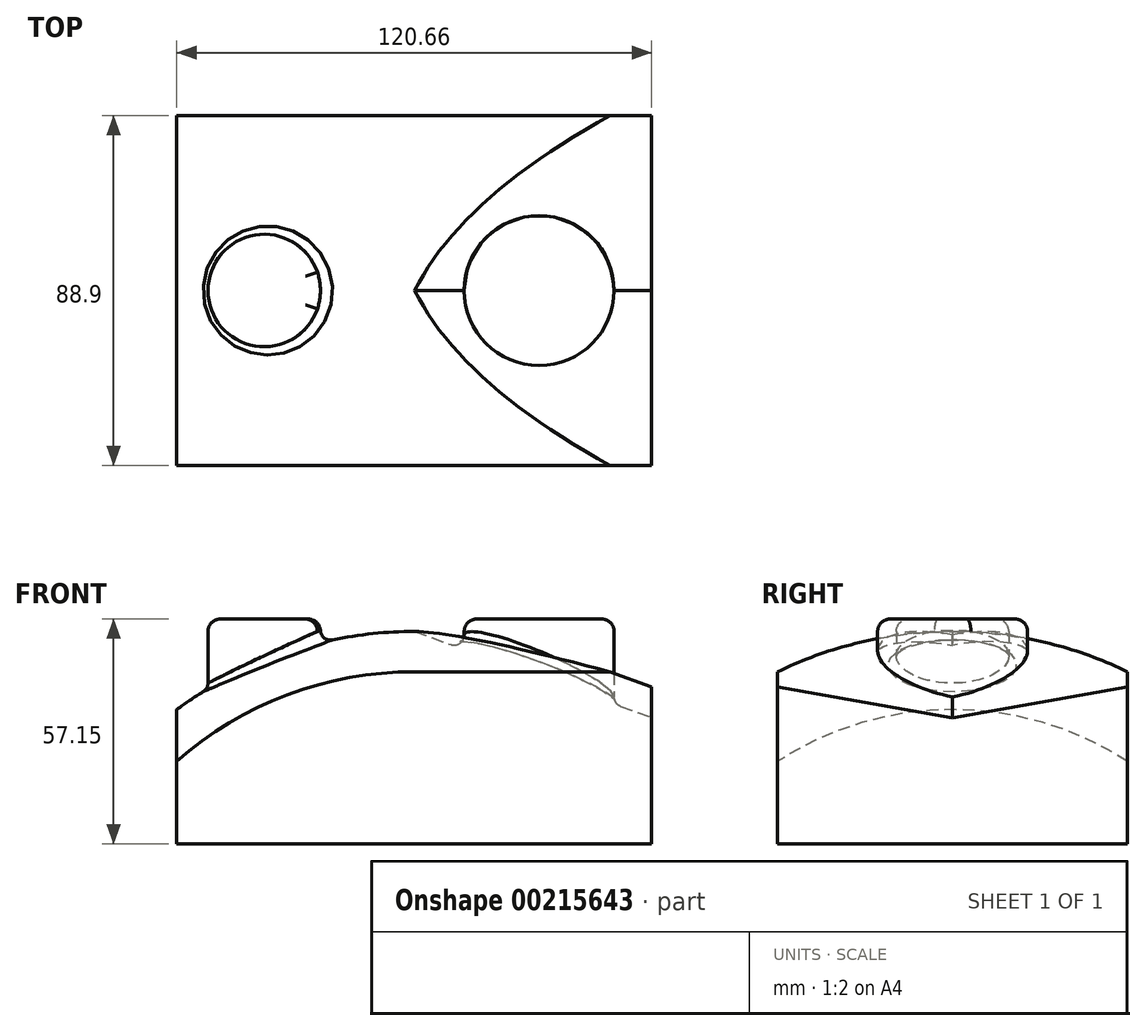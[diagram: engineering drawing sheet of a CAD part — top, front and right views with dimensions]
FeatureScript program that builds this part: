
annotation { "Feature Type Name" : "Feature", "Feature Type Description" : "" }
export const myFeature = defineFeature(function(context is Context, id is Id, definition is map)
    precondition{}
    {
        {
            var Q0;
            Q0=qCreatedBy(makeId("Top.planeOp"),FACE);
            var sketch = newSketch(context, id + "F0", { "sketchPlane" : qUnion([Q0])});
            skLineSegment(sketch, "E0.bottom", {"start": v(60.33, -44.45) * mm, "end": v(-60.33, -44.45) * mm});
            skLineSegment(sketch, "E0.top", {"start": v(60.33, 44.45) * mm, "end": v(-60.33, 44.45) * mm});
            skLineSegment(sketch, "E0.left", {"start": v(60.33, -44.45) * mm, "end": v(60.33, 44.45) * mm});
            skLineSegment(sketch, "E0.right", {"start": v(-60.33, -44.45) * mm, "end": v(-60.33, 44.45) * mm});
            skPoint(sketch, "E0.middle", {"position": v(0, 0) * mm});
            skSolve(sketch);
        }
        {
            var Q0;
            Q0 = qSketchRegion(id + "F0", true);
            extrude(context, id + "F1", {"entities" : qUnion([Q0]), "depth" : 53.97 * mm});
        }
        {
            var Q0;
            Q0=qCreatedBy(makeId("Front.planeOp"),FACE);
            var sketch = newSketch(context, id + "F2", { "sketchPlane" : qUnion([Q0])});
            skLineSegment(sketch, "E1", {"start": v(106.64, 12.85) * mm, "end": v(-12.7, 56.29) * mm});
            skSolve(sketch);
        }
        {
            var Q0;
            Q0=qCreatedBy(makeId("Right.planeOp"),FACE);
            var Q1;
            Q1=sQuery(id+"F2.wireOp",VERTEX,"E1.end");
            cPlane(context, id + "F3", {"entities" : qUnion([Q0, Q1]), "cplaneType" : CPlaneType.PLANE_POINT, "offset" : 25.4 * mm, "width" : 152.4 * mm, "height" : 152.4 * mm});
        }
        {
            var Q0;
            Q0=qCreatedBy(id+"F3.planeOp",FACE);
            var sketch = newSketch(context, id + "F4", { "sketchPlane" : qUnion([Q0])});
            skLineSegment(sketch, "E2", {"start": v(0, 58.65) * mm, "end": v(63.52, 69.85) * mm});
            skLineSegment(sketch, "E3", {"start": v(-63.52, 69.85) * mm, "end": v(0, 58.65) * mm});
            skLineSegment(sketch, "E4", {"start": v(-63.52, 69.85) * mm, "end": v(-63.52, 114.3) * mm});
            skLineSegment(sketch, "E5", {"start": v(-63.52, 114.3) * mm, "end": v(63.48, 114.3) * mm});
            skLineSegment(sketch, "E6", {"start": v(63.48, 114.3) * mm, "end": v(63.52, 69.85) * mm});
            skSolve(sketch);
        }
        {
            var Q0;
            Q0 = qSketchRegion(id + "F4", true);
            var Q1;
            Q1 = qConstructionFilter(qBodyType(qCreatedBy(id + "F2" ,EDGE), BodyType.WIRE), ConstructionObject.NO);
            sweep(context, id + "F5", {"operationType" : NewBodyOperationType.REMOVE, "profiles" : qUnion([Q0]), "path" : qUnion([Q1])});
        }
        {
            var Q0;
            Q0=qCreatedBy(makeId("Front.planeOp"),FACE);
            var sketch = newSketch(context, id + "F6", { "sketchPlane" : qUnion([Q0])});
            skArc(sketch, "E7", {"start": v(0, 53.98) * mm, "mid": v(-41.8, 44.98) * mm, "end": v(-76.2, 19.58) * mm});
            skLineSegment(sketch, "E8", {"start": v(0, 71.33) * mm, "end": v(0, 13.76) * mm, "construction": true});
            skLineSegment(sketch, "E9", {"start": v(0, 53.98) * mm, "end": v(0, 66.67) * mm});
            skLineSegment(sketch, "E10", {"start": v(0, 66.67) * mm, "end": v(-76.2, 66.67) * mm});
            skLineSegment(sketch, "E11", {"start": v(-76.2, 66.67) * mm, "end": v(-76.2, 19.58) * mm});
            skSolve(sketch);
        }
        {
            var Q0;
            Q0 = qSketchRegion(id + "F6", true);
            var Q1;
            Q1=sQuery(id+"F6.wireOp",EDGE,"E8");
            revolve(context, id + "F7", {"operationType" : NewBodyOperationType.REMOVE, "entities" : qUnion([Q0]), "axis" : qUnion([Q1]), "revolveType" : RevolveType.SYMMETRIC, "angle" : 180 * degree});
        }
        {
            var Q0;
            Q0=qCreatedBy(makeId("Right.planeOp"),FACE);
            var sketch = newSketch(context, id + "F8", { "sketchPlane" : qUnion([Q0])});
            skLineSegment(sketch, "E12", {"start": v(44.45, 43.74) * mm, "end": v(44.45, 69.14) * mm});
            skLineSegment(sketch, "E13", {"start": v(44.45, 69.14) * mm, "end": v(-44.45, 69.14) * mm});
            skLineSegment(sketch, "E14", {"start": v(-44.45, 69.14) * mm, "end": v(-44.45, 43.74) * mm});
            skArc(sketch, "E15.0", {"start": v(-44.45, 43.74) * mm, "mid": v(-22.8, 51.38) * mm, "end": v(0, 53.98) * mm});
            skArc(sketch, "E16.0", {"start": v(0, 53.98) * mm, "mid": v(22.8, 51.38) * mm, "end": v(44.45, 43.74) * mm});
            skPoint(sketch, "E17.orphan", {"position": v(-44.45, 20.99) * mm});
            skSolve(sketch);
        }
        {
            var Q0;
            Q0 = qSketchRegion(id + "F8", true);
            extrude(context, id + "F9", {"entities" : qUnion([Q0]), "operationType" : NewBodyOperationType.REMOVE, "endBound" : BoundingType.THROUGH_ALL, "depth" : 25.4 * mm});
        }
        {
            var Q0;
            Q0=qCreatedBy(makeId("Top.planeOp"),FACE);
            var sketch = newSketch(context, id + "F10", { "sketchPlane" : qUnion([Q0])});
            skCircle(sketch, "E18", {"center": v(31.75, 0) * mm, "radius": 19.05 * mm});
            skCircle(sketch, "E19", {"center": v(-38.1, 0) * mm, "radius": 14.29 * mm});
            skSolve(sketch);
        }
        {
            var Q0;
            Q0 = qSketchRegion(id + "F10", true);
            extrude(context, id + "F11", {"entities" : qUnion([Q0]), "operationType" : NewBodyOperationType.ADD, "depth" : 57.15 * mm});
        }
        {
            var Q0;
            Q0=makeQuery(id+"F11.boolean.opBoolean","INTERSECT",EDGE,{"derivedFrom":[makeQuery(id+"F5.boolean.opBoolean","COPY",FACE,{"derivedFrom":makeQuery(id+"F5.opSweep","SWEPT_FACE",FACE,{"disambiguationData":[OSD([sQuery(id+"F2.wireOp",EDGE,"E1"),sQuery(id+"F4.wireOp",EDGE,"E2")])]})}),makeQuery(id+"F11.opExtrude","SWEPT_FACE",FACE,{"disambiguationData":[OSD([sQuery(id+"F10.wireOp",EDGE,"E18")])]})]});
            var Q1;
            Q1=makeQuery(id+"F11.boolean.opBoolean","INTERSECT",EDGE,{"derivedFrom":[makeQuery(id+"F7.boolean.opBoolean","COPY",FACE,{"derivedFrom":makeQuery(id+"F7.opRevolve","SWEPT_FACE",FACE,{"disambiguationData":[OSD([sQuery(id+"F6.wireOp",EDGE,"E7")])]})}),makeQuery(id+"F11.opExtrude","SWEPT_FACE",FACE,{"disambiguationData":[OSD([sQuery(id+"F10.wireOp",EDGE,"E19")])]})]});
            var Q2;
            Q2=makeQuery(id+"F11.boolean.opBoolean","INTERSECT",EDGE,{"derivedFrom":[makeQuery(id+"F5.boolean.opBoolean","COPY",FACE,{"derivedFrom":makeQuery(id+"F5.opSweep","SWEPT_FACE",FACE,{"disambiguationData":[OSD([sQuery(id+"F2.wireOp",EDGE,"E1"),sQuery(id+"F4.wireOp",EDGE,"E3")])]})}),makeQuery(id+"F11.opExtrude","SWEPT_FACE",FACE,{"disambiguationData":[OSD([sQuery(id+"F10.wireOp",EDGE,"E18")])]})]});
            fillet(context, id + "F12", {"entities" : qUnion([Q0, Q1, Q2]), "radius" : 2.54 * mm, "tangentPropagation" : true, "allowEdgeOverflow" : false});
        }
        {
            var Q0;
            Q0=makeQuery(id+"F11.opExtrude","CAP_EDGE",EDGE,{"disambiguationData":[OSD([sQuery(id+"F10.wireOp",EDGE,"E18")])],"isStart":false});
            var Q1;
            Q1=makeQuery(id+"F11.opExtrude","CAP_EDGE",EDGE,{"disambiguationData":[OSD([sQuery(id+"F10.wireOp",EDGE,"E19")])],"isStart":false});
            fillet(context, id + "F13", {"entities" : qUnion([Q0, Q1]), "radius" : 3.17 * mm, "tangentPropagation" : true, "allowEdgeOverflow" : false});
        }
    });
